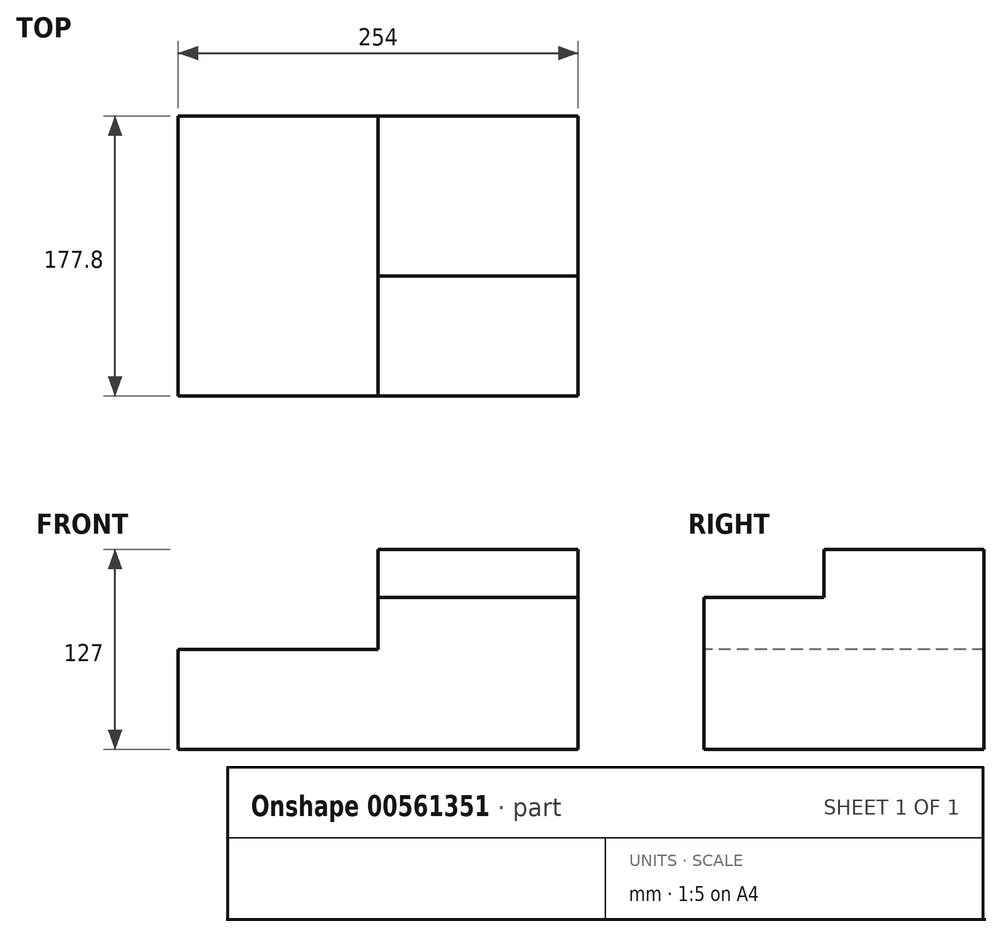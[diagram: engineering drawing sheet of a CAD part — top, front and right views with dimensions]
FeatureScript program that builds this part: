
annotation { "Feature Type Name" : "Feature", "Feature Type Description" : "" }
export const myFeature = defineFeature(function(context is Context, id is Id, definition is map)
    precondition{}
    {
        {
            var Q0;
            Q0=qCreatedBy(makeId("Top.planeOp"),FACE);
            var sketch = newSketch(context, id + "F0", { "sketchPlane" : qUnion([Q0])});
            skLineSegment(sketch, "E0.bottom", {"start": v(127, 88.9) * mm, "end": v(-127, 88.9) * mm});
            skLineSegment(sketch, "E0.top", {"start": v(127, -88.9) * mm, "end": v(-127, -88.9) * mm});
            skLineSegment(sketch, "E0.left", {"start": v(127, 88.9) * mm, "end": v(127, -88.9) * mm});
            skLineSegment(sketch, "E0.right", {"start": v(-127, 88.9) * mm, "end": v(-127, -88.9) * mm});
            skPoint(sketch, "E0.middle", {"position": v(0, 0) * mm});
            skSolve(sketch);
        }
        {
            var Q0;
            Q0 = qSketchRegion(id + "F0", true);
            extrude(context, id + "F1", {"entities" : qUnion([Q0]), "depth" : 63.5 * mm, "offsetDistance" : 25.4 * mm});
        }
        {
            var Q0;
            Q0=makeQuery(id+"F1.opExtrude","CAP_FACE",FACE,{"disambiguationData":[OSD([sQuery(id+"F0.wireOp",EDGE,"E0.bottom"),sQuery(id+"F0.wireOp",EDGE,"E0.top"),sQuery(id+"F0.wireOp",EDGE,"E0.left"),sQuery(id+"F0.wireOp",EDGE,"E0.right")])],"isStart":false});
            var sketch = newSketch(context, id + "F2", { "sketchPlane" : qUnion([Q0])});
            skLineSegment(sketch, "E1.bottom", {"start": v(127, 88.9) * mm, "end": v(0, 88.9) * mm});
            skLineSegment(sketch, "E1.top", {"start": v(127, -88.9) * mm, "end": v(0, -88.9) * mm});
            skLineSegment(sketch, "E1.left", {"start": v(127, 88.9) * mm, "end": v(127, -88.9) * mm});
            skLineSegment(sketch, "E1.right", {"start": v(0, 88.9) * mm, "end": v(0, -88.9) * mm});
            skSolve(sketch);
        }
        {
            var Q0;
            Q0 = qSketchRegion(id + "F2", true);
            extrude(context, id + "F3", {"entities" : qUnion([Q0]), "operationType" : NewBodyOperationType.ADD, "depth" : 33.02 * mm, "offsetDistance" : 25.4 * mm});
        }
        {
            var Q0;
            Q0=makeQuery(id+"F3.opExtrude","CAP_FACE",FACE,{"disambiguationData":[OSD([sQuery(id+"F2.wireOp",EDGE,"E1.bottom"),sQuery(id+"F2.wireOp",EDGE,"E1.top"),sQuery(id+"F2.wireOp",EDGE,"E1.left"),sQuery(id+"F2.wireOp",EDGE,"E1.right")])],"isStart":false});
            var sketch = newSketch(context, id + "F4", { "sketchPlane" : qUnion([Q0])});
            skLineSegment(sketch, "E2.bottom", {"start": v(127, 88.9) * mm, "end": v(0, 88.9) * mm});
            skLineSegment(sketch, "E2.top", {"start": v(127, -12.7) * mm, "end": v(0, -12.7) * mm});
            skLineSegment(sketch, "E2.left", {"start": v(127, 88.9) * mm, "end": v(127, -12.7) * mm});
            skLineSegment(sketch, "E2.right", {"start": v(0, 88.9) * mm, "end": v(0, -12.7) * mm});
            skSolve(sketch);
        }
        {
            var Q0;
            Q0 = qSketchRegion(id + "F4", true);
            extrude(context, id + "F5", {"entities" : qUnion([Q0]), "operationType" : NewBodyOperationType.ADD, "depth" : 30.48 * mm, "offsetDistance" : 25.4 * mm});
        }
    });
